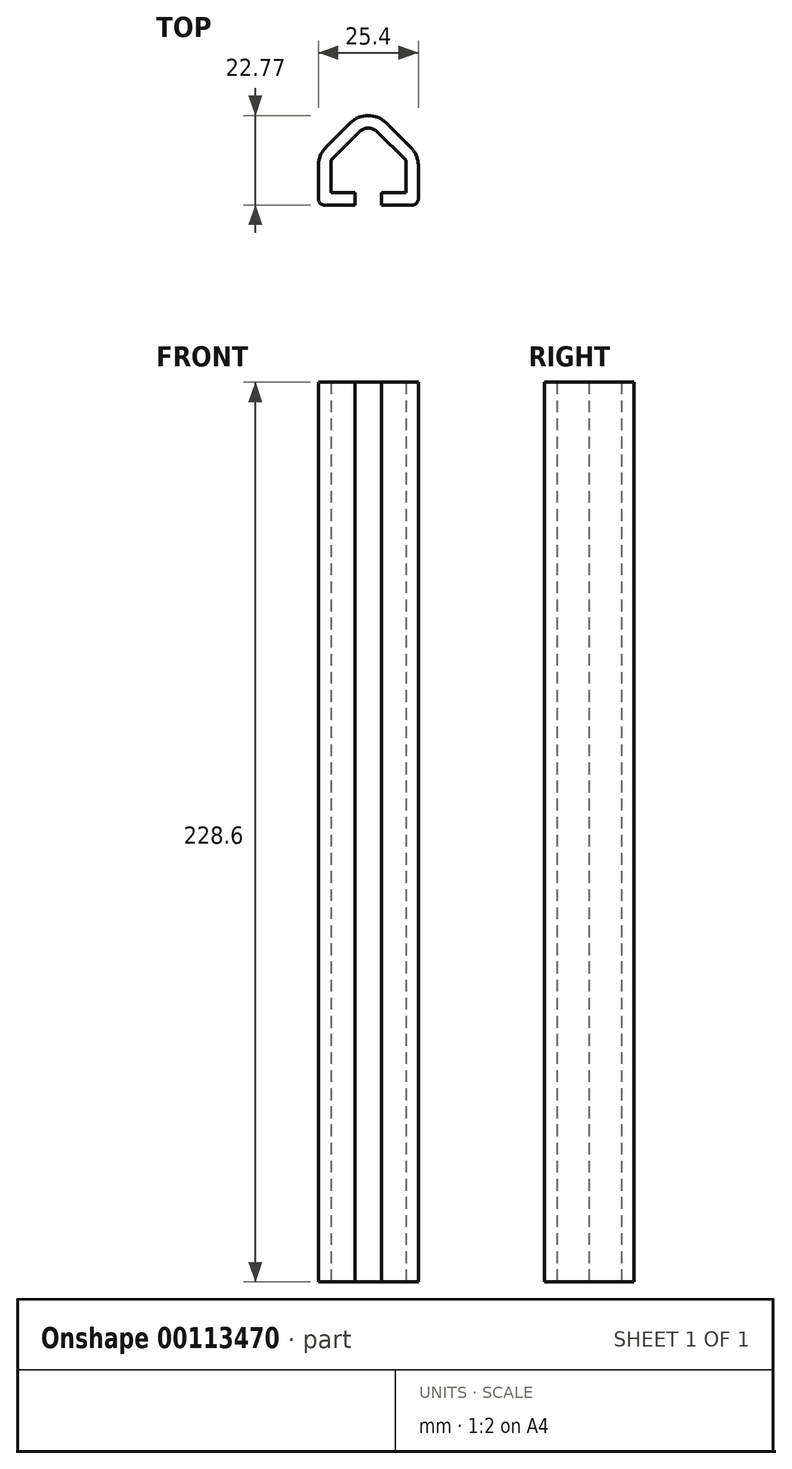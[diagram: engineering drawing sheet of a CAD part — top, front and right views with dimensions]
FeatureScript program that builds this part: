
annotation { "Feature Type Name" : "Feature", "Feature Type Description" : "" }
export const myFeature = defineFeature(function(context is Context, id is Id, definition is map)
    precondition{}
    {
        {
            var Q0;
            Q0=qCreatedBy(makeId("Top.planeOp"),FACE);
            var sketch = newSketch(context, id + "F0", { "sketchPlane" : qUnion([Q0])});
            skLineSegment(sketch, "E0.top", {"start": v(-11.11, -12.7) * mm, "end": v(-3.37, -12.7) * mm});
            skLineSegment(sketch, "E0.left", {"start": v(-12.7, -2.63) * mm, "end": v(-12.7, -11.11) * mm});
            skLineSegment(sketch, "E0.right", {"start": v(12.7, -2.63) * mm, "end": v(12.7, -11.11) * mm});
            skPoint(sketch, "E0.middle", {"position": v(0, 0) * mm});
            skLineSegment(sketch, "E1", {"start": v(-10.84, 1.86) * mm, "end": v(-4.5, 8.2) * mm});
            skLineSegment(sketch, "E2", {"start": v(4.5, 8.2) * mm, "end": v(10.84, 1.86) * mm});
            skPoint(sketch, "E3.visualSharp", {"position": v(0, 12.7) * mm});
            skArc(sketch, "E3.filletArc", {"start": v(4.5, 8.2) * mm, "mid": v(0, 10.07) * mm, "end": v(-4.5, 8.2) * mm});
            skPoint(sketch, "E4.orphan", {"position": v(12.7, 12.7) * mm});
            skPoint(sketch, "E5.orphan", {"position": v(-12.7, 12.7) * mm});
            skLineSegment(sketch, "E6.left", {"start": v(3.37, -9.53) * mm, "end": v(3.37, -12.7) * mm});
            skPoint(sketch, "E6.middle", {"position": v(0, -7.05) * mm});
            skLineSegment(sketch, "E7.trimOffspring", {"start": v(3.37, -12.7) * mm, "end": v(11.11, -12.7) * mm});
            skPoint(sketch, "E8.orphan", {"position": v(-3.37, -18.19) * mm});
            skPoint(sketch, "E9.orphan", {"position": v(3.37, -18.19) * mm});
            skLineSegment(sketch, "E10.top", {"start": v(-9.53, -9.53) * mm, "end": v(-3.37, -9.53) * mm});
            skLineSegment(sketch, "E10.left", {"start": v(-9.53, -1.32) * mm, "end": v(-9.53, -9.53) * mm});
            skLineSegment(sketch, "E10.right", {"start": v(9.53, -1.32) * mm, "end": v(9.53, -9.53) * mm});
            skLineSegment(sketch, "E11", {"start": v(-9.53, -1.32) * mm, "end": v(-2.25, 5.96) * mm});
            skLineSegment(sketch, "E12.trimOffspring", {"start": v(-3.37, -9.53) * mm, "end": v(-3.37, -12.7) * mm});
            skPoint(sketch, "E6.right.start.orphan", {"position": v(-3.37, 4.08) * mm});
            skPoint(sketch, "E13.orphan", {"position": v(3.37, 4.08) * mm});
            skLineSegment(sketch, "E14.trimOffspring", {"start": v(3.37, -9.53) * mm, "end": v(9.53, -9.53) * mm});
            skPoint(sketch, "E15.visualSharp", {"position": v(-12.7, 0) * mm});
            skArc(sketch, "E15.filletArc", {"start": v(-10.84, 1.86) * mm, "mid": v(-12.22, -0.2) * mm, "end": v(-12.7, -2.63) * mm});
            skPoint(sketch, "E16.visualSharp", {"position": v(12.7, 0) * mm});
            skArc(sketch, "E16.filletArc", {"start": v(12.7, -2.63) * mm, "mid": v(12.22, -0.2) * mm, "end": v(10.84, 1.86) * mm});
            skLineSegment(sketch, "E17", {"start": v(2.25, 5.96) * mm, "end": v(9.53, -1.32) * mm});
            skArc(sketch, "E18.filletArc", {"start": v(2.25, 5.96) * mm, "mid": v(0, 6.9) * mm, "end": v(-2.25, 5.96) * mm});
            skPoint(sketch, "E19.visualSharp", {"position": v(-12.7, -12.7) * mm});
            skArc(sketch, "E19.filletArc", {"start": v(-12.7, -11.11) * mm, "mid": v(-12.24, -12.24) * mm, "end": v(-11.11, -12.7) * mm});
            skPoint(sketch, "E20.visualSharp", {"position": v(12.7, -12.7) * mm});
            skArc(sketch, "E20.filletArc", {"start": v(11.11, -12.7) * mm, "mid": v(12.24, -12.24) * mm, "end": v(12.7, -11.11) * mm});
            skSolve(sketch);
        }
        {
            var Q0;
            Q0=makeQuery(id+"F0.imprint","IMPRINT",FACE,{"disambiguationData":[TD([[makeQuery(id+"F0.imprint","IMPRINT",EDGE,{"derivedFrom":sQuery(id+"F0.wireOp",EDGE,"E0.top")}),1.0]])]});
            extrude(context, id + "F1", {"entities" : qUnion([Q0]), "depth" : 228.6 * mm});
        }
    });
